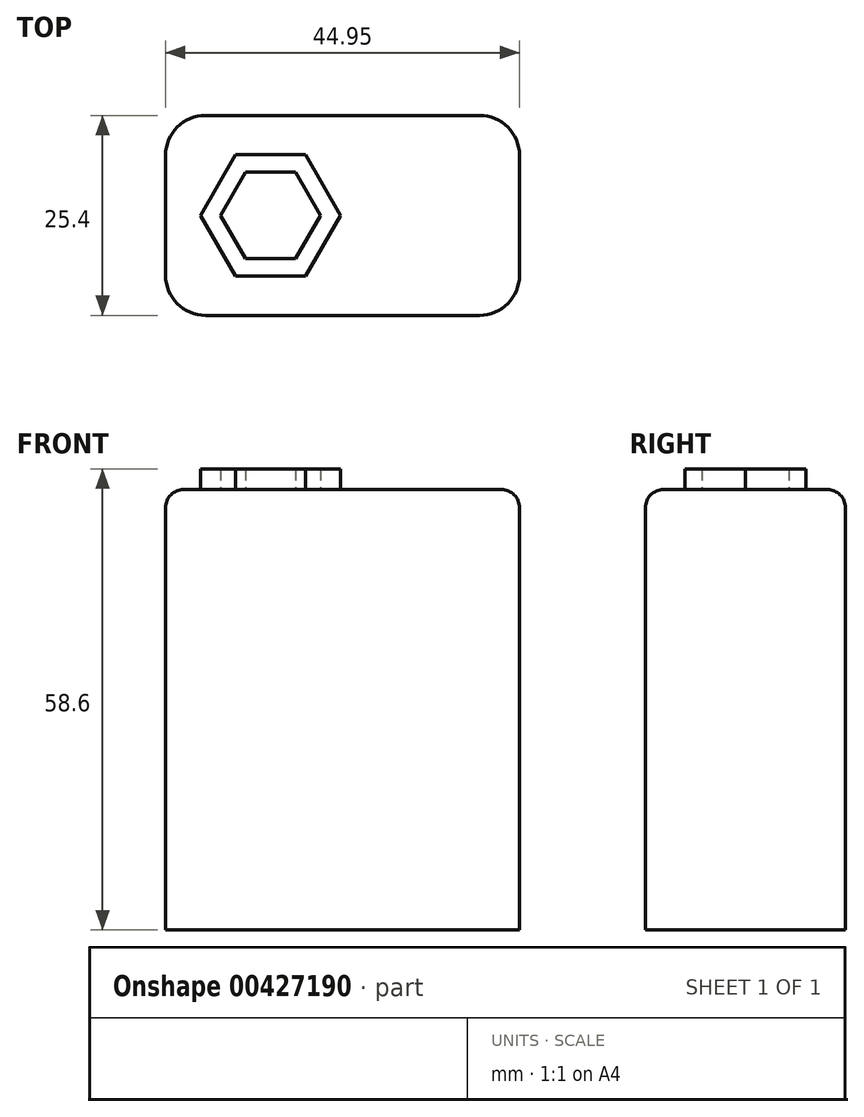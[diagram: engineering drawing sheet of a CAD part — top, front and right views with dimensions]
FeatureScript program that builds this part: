
annotation { "Feature Type Name" : "Feature", "Feature Type Description" : "" }
export const myFeature = defineFeature(function(context is Context, id is Id, definition is map)
    precondition{}
    {
        {
            var Q0;
            Q0=qCreatedBy(makeId("Front.planeOp"),FACE);
            var sketch = newSketch(context, id + "F0", { "sketchPlane" : qUnion([Q0])});
            skLineSegment(sketch, "E0.bottom", {"start": v(0, 0) * mm, "end": v(-44.95, 0) * mm});
            skLineSegment(sketch, "E0.top", {"start": v(0, 55.96) * mm, "end": v(-44.95, 55.96) * mm});
            skLineSegment(sketch, "E0.left", {"start": v(0, 0) * mm, "end": v(0, 55.96) * mm});
            skLineSegment(sketch, "E0.right", {"start": v(-44.95, 0) * mm, "end": v(-44.95, 55.96) * mm});
            skSolve(sketch);
        }
        {
            var Q0;
            Q0=makeQuery(id+"F0.imprint","IMPRINT",FACE,{"disambiguationData":[TD([[makeQuery(id+"F0.imprint","IMPRINT",EDGE,{"derivedFrom":sQuery(id+"F0.wireOp",EDGE,"E0.bottom")}),-1.0]])]});
            extrude(context, id + "F1", {"entities" : qUnion([Q0]), "depth" : 25.4 * mm});
        }
        {
            var Q0;
            Q0=makeQuery(id+"F1.opExtrude","CAP_EDGE",EDGE,{"disambiguationData":[OSD([sQuery(id+"F0.wireOp",EDGE,"E0.right")])],"isStart":false});
            var Q1;
            Q1=makeQuery(id+"F1.opExtrude","CAP_EDGE",EDGE,{"disambiguationData":[OSD([sQuery(id+"F0.wireOp",EDGE,"E0.right")])],"isStart":true});
            var Q2;
            Q2=makeQuery(id+"F1.opExtrude","CAP_EDGE",EDGE,{"disambiguationData":[OSD([sQuery(id+"F0.wireOp",EDGE,"E0.left")])],"isStart":false});
            var Q3;
            Q3=makeQuery(id+"F1.opExtrude","CAP_EDGE",EDGE,{"disambiguationData":[OSD([sQuery(id+"F0.wireOp",EDGE,"E0.left")])],"isStart":true});
            fillet(context, id + "F2", {"entities" : qUnion([Q0, Q1, Q2, Q3]), "radius" : 5.08 * mm, "tangentPropagation" : true, "allowEdgeOverflow" : false});
        }
        {
            var Q0;
            Q0=makeQuery(id+"F1.opExtrude","SWEPT_FACE",FACE,{"disambiguationData":[OSD([sQuery(id+"F0.wireOp",EDGE,"E0.top")])]});
            var sketch = newSketch(context, id + "F3", { "sketchPlane" : qUnion([Q0])});
            skCircle(sketch, "E1.cCircle", {"center": v(-31.63, -12.7) * mm, "radius": 8.89 * mm, "construction": true});
            skLineSegment(sketch, "E1.0", {"start": v(-22.74, -12.7) * mm, "end": v(-27.19, -20.4) * mm});
            skLineSegment(sketch, "E1.1", {"start": v(-27.19, -20.4) * mm, "end": v(-36.08, -20.4) * mm});
            skLineSegment(sketch, "E1.2", {"start": v(-36.08, -20.4) * mm, "end": v(-40.52, -12.7) * mm});
            skLineSegment(sketch, "E1.3", {"start": v(-40.52, -12.7) * mm, "end": v(-36.08, -5) * mm});
            skLineSegment(sketch, "E1.4", {"start": v(-36.08, -5) * mm, "end": v(-27.19, -5) * mm});
            skLineSegment(sketch, "E1.5", {"start": v(-27.19, -5) * mm, "end": v(-22.74, -12.7) * mm});
            skSolve(sketch);
        }
        {
            var Q0;
            Q0=makeQuery(id+"F1.opExtrude","SWEPT_FACE",FACE,{"disambiguationData":[OSD([sQuery(id+"F0.wireOp",EDGE,"E0.top")])]});
            var sketch = newSketch(context, id + "F4", { "sketchPlane" : qUnion([Q0])});
            skCircle(sketch, "E2", {"center": v(-12.82, -13.8) * mm, "radius": 7.31 * mm});
            skSolve(sketch);
        }
        {
            var Q0;
            Q0=sQuery(id+"F4.wireOp",EDGE,"E2");
            extrude(context, id + "F5", {"bodyType" : ToolBodyType.SURFACE, "surfaceEntities" : qUnion([Q0]), "depth" : 2.54 * mm});
        }
        {
            var Q0;
            Q0=makeQuery(id+"F1.opExtrude","SWEPT_FACE",FACE,{"disambiguationData":[OSD([sQuery(id+"F0.wireOp",EDGE,"E0.top")])]});
            var sketch = newSketch(context, id + "F6", { "sketchPlane" : qUnion([Q0])});
            skCircle(sketch, "E3.cCircle", {"center": v(-31.63, -12.7) * mm, "radius": 5.5 * mm, "construction": true});
            skLineSegment(sketch, "E3.0", {"start": v(-37.98, -12.7) * mm, "end": v(-34.8, -7.2) * mm});
            skLineSegment(sketch, "E3.1", {"start": v(-34.8, -7.2) * mm, "end": v(-28.46, -7.2) * mm});
            skLineSegment(sketch, "E3.2", {"start": v(-28.46, -7.2) * mm, "end": v(-25.28, -12.7) * mm});
            skLineSegment(sketch, "E3.3", {"start": v(-25.28, -12.7) * mm, "end": v(-28.46, -18.2) * mm});
            skLineSegment(sketch, "E3.4", {"start": v(-28.46, -18.2) * mm, "end": v(-34.8, -18.2) * mm});
            skLineSegment(sketch, "E3.5", {"start": v(-34.8, -18.2) * mm, "end": v(-37.98, -12.7) * mm});
            skPoint(sketch, "E3.0.midPoint", {"position": v(-36.4, -9.95) * mm});
            skLineSegment(sketch, "E4.0", {"start": v(-40.52, -12.7) * mm, "end": v(-36.08, -5) * mm});
            skLineSegment(sketch, "E5.0", {"start": v(-36.08, -5) * mm, "end": v(-27.19, -5) * mm});
            skPoint(sketch, "E6.0", {"position": v(-24.96, -8.85) * mm});
            skLineSegment(sketch, "E7.0", {"start": v(-27.19, -5) * mm, "end": v(-22.74, -12.7) * mm});
            skLineSegment(sketch, "E8.0", {"start": v(-22.74, -12.7) * mm, "end": v(-27.19, -20.4) * mm});
            skLineSegment(sketch, "E9.0", {"start": v(-27.19, -20.4) * mm, "end": v(-36.08, -20.4) * mm});
            skLineSegment(sketch, "E10.0", {"start": v(-36.08, -20.4) * mm, "end": v(-40.52, -12.7) * mm});
            skSolve(sketch);
        }
        {
            var Q0;
            Q0 = qSketchRegion(id + "F6", true);
            extrude(context, id + "F7", {"entities" : qUnion([Q0]), "operationType" : NewBodyOperationType.ADD, "depth" : 2.64 * mm});
        }
        {
            var Q0;
            Q0=makeQuery(id+"F1.opExtrude","CAP_EDGE",EDGE,{"disambiguationData":[OSD([sQuery(id+"F0.wireOp",EDGE,"E0.top")])],"isStart":false});
            fillet(context, id + "F8", {"entities" : qUnion([Q0]), "radius" : 2.3 * mm, "tangentPropagation" : true, "allowEdgeOverflow" : false});
        }
    });
